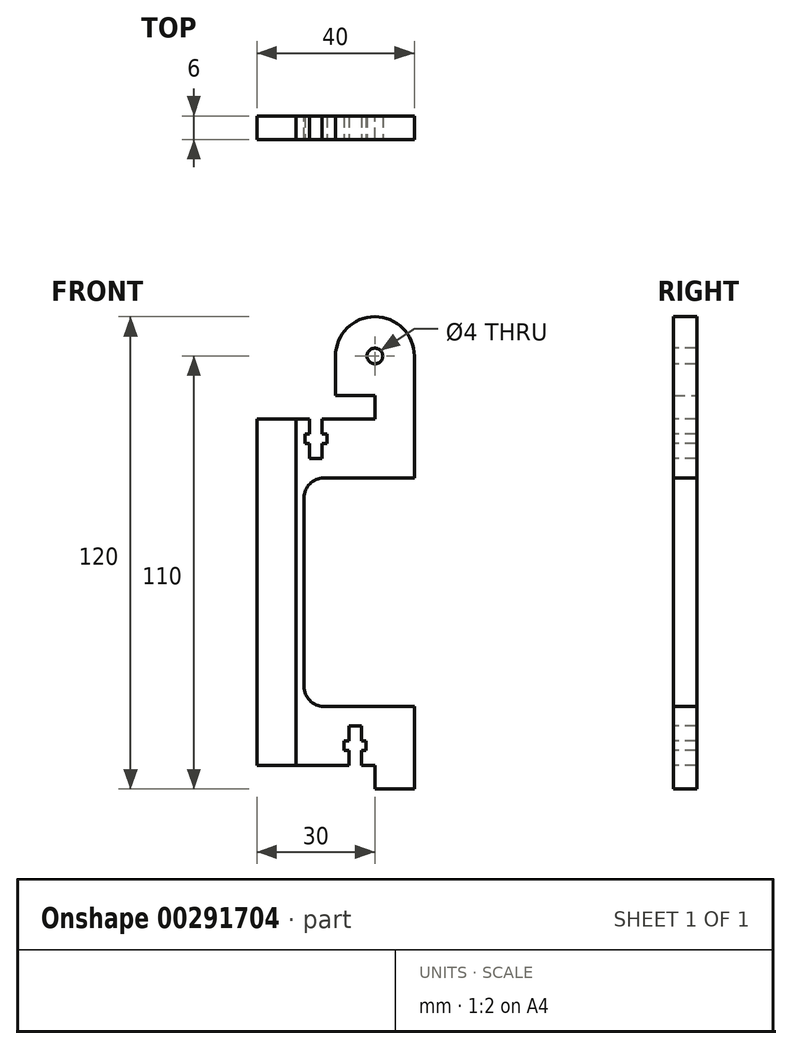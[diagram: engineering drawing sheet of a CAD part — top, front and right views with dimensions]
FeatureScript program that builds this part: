
annotation { "Feature Type Name" : "Feature", "Feature Type Description" : "" }
export const myFeature = defineFeature(function(context is Context, id is Id, definition is map)
    precondition{}
    {
        {
            var Q0;
            Q0=qCreatedBy(makeId("Front.planeOp"),FACE);
            var sketch = newSketch(context, id + "F0", { "sketchPlane" : qUnion([Q0])});
            skLineSegment(sketch, "E0", {"start": v(0, 0) * mm, "end": v(-10, 0) * mm});
            skLineSegment(sketch, "E1", {"start": v(-10, 0) * mm, "end": v(-10, 6) * mm});
            skLineSegment(sketch, "E2", {"start": v(-10, 6) * mm, "end": v(-30, 6) * mm});
            skLineSegment(sketch, "E3", {"start": v(-30, 6) * mm, "end": v(-30, 94) * mm});
            skLineSegment(sketch, "E4", {"start": v(-30, 94) * mm, "end": v(-10, 94) * mm});
            skLineSegment(sketch, "E5", {"start": v(-10, 94) * mm, "end": v(-10, 100) * mm});
            skLineSegment(sketch, "E6", {"start": v(0, 110) * mm, "end": v(0, 0) * mm});
            skLineSegment(sketch, "E7", {"start": v(-10, 100) * mm, "end": v(-20, 100) * mm});
            skLineSegment(sketch, "E8", {"start": v(-20, 100) * mm, "end": v(-20, 110) * mm});
            skArc(sketch, "E9", {"start": v(0, 110) * mm, "mid": v(-10, 120) * mm, "end": v(-20, 110) * mm});
            skLineSegment(sketch, "E10", {"start": v(-20, 110) * mm, "end": v(0, 110) * mm, "construction": true});
            skSolve(sketch);
        }
        {
            var Q0;
            Q0=qSketchRegion(id+"F0",true);
            extrude(context, id + "F1", {"entities" : qUnion([Q0]), "depth" : 6 * mm});
        }
        {
            var Q0;
            Q0=makeQuery(id+"F1.opExtrude","CAP_FACE",FACE,{"disambiguationData":[OSD([sQuery(id+"F0.wireOp",EDGE,"E0"),sQuery(id+"F0.wireOp",EDGE,"E1"),sQuery(id+"F0.wireOp",EDGE,"E2"),sQuery(id+"F0.wireOp",EDGE,"E3"),sQuery(id+"F0.wireOp",EDGE,"E4"),sQuery(id+"F0.wireOp",EDGE,"E5"),sQuery(id+"F0.wireOp",EDGE,"Jmk1pW6G-ZqLD-Fl2S-BXqT-ifLrlO1WaDic"),sQuery(id+"F0.wireOp",EDGE,"E6")])],"isStart":false});
            var sketch = newSketch(context, id + "F2", { "sketchPlane" : qUnion([Q0])});
            skLineSegment(sketch, "E11", {"start": v(-30, 50) * mm, "end": v(0, 50) * mm, "construction": true});
            skLineSegment(sketch, "E12", {"start": v(-10, 6) * mm, "end": v(-10, 94) * mm, "construction": true});
            skLineSegment(sketch, "E13", {"start": v(-15, 6) * mm, "end": v(-15, 50) * mm, "construction": true});
            skLineSegment(sketch, "E14", {"start": v(-15, 6) * mm, "end": v(-16.6, 6) * mm});
            skLineSegment(sketch, "E15", {"start": v(-16.6, 6) * mm, "end": v(-16.6, 9.75) * mm});
            skLineSegment(sketch, "E16", {"start": v(-16.6, 9.75) * mm, "end": v(-17.8, 9.75) * mm});
            skLineSegment(sketch, "E17", {"start": v(-17.8, 9.75) * mm, "end": v(-17.8, 12.25) * mm});
            skLineSegment(sketch, "E18", {"start": v(-17.8, 12.25) * mm, "end": v(-16.6, 12.25) * mm});
            skLineSegment(sketch, "E19", {"start": v(-16.6, 12.25) * mm, "end": v(-16.6, 16) * mm});
            skLineSegment(sketch, "E20", {"start": v(-16.6, 16) * mm, "end": v(-15, 16) * mm});
            skLineSegment(sketch, "E21.MirrorCS", {"start": v(-12.2, 12.25) * mm, "end": v(-13.4, 12.25) * mm});
            skLineSegment(sketch, "E22.MirrorCS", {"start": v(-12.2, 9.75) * mm, "end": v(-12.2, 12.25) * mm});
            skLineSegment(sketch, "E23.MirrorCS", {"start": v(-13.4, 12.25) * mm, "end": v(-13.4, 16) * mm});
            skLineSegment(sketch, "E24.MirrorCS", {"start": v(-13.4, 16) * mm, "end": v(-15, 16) * mm});
            skLineSegment(sketch, "E25.MirrorCS", {"start": v(-13.4, 9.75) * mm, "end": v(-12.2, 9.75) * mm});
            skLineSegment(sketch, "E26.MirrorCS", {"start": v(-15, 6) * mm, "end": v(-13.4, 6) * mm});
            skLineSegment(sketch, "E27.MirrorCS", {"start": v(-13.4, 6) * mm, "end": v(-13.4, 9.75) * mm});
            skLineSegment(sketch, "E28.MirrorCS", {"start": v(-10, 34) * mm, "end": v(-10, -54) * mm, "construction": true});
            skLineSegment(sketch, "E29", {"start": v(-25, 94) * mm, "end": v(-25, 50) * mm, "construction": true});
            skLineSegment(sketch, "E30", {"start": v(-25, 94) * mm, "end": v(-26.6, 94) * mm});
            skLineSegment(sketch, "E31", {"start": v(-26.6, 94) * mm, "end": v(-26.6, 90.25) * mm});
            skLineSegment(sketch, "E32", {"start": v(-26.6, 90.25) * mm, "end": v(-27.8, 90.25) * mm});
            skLineSegment(sketch, "E33", {"start": v(-27.8, 90.25) * mm, "end": v(-27.8, 87.75) * mm});
            skLineSegment(sketch, "E34", {"start": v(-27.8, 87.75) * mm, "end": v(-26.6, 87.75) * mm});
            skLineSegment(sketch, "E35", {"start": v(-26.6, 87.75) * mm, "end": v(-26.6, 84) * mm});
            skLineSegment(sketch, "E36", {"start": v(-26.6, 84) * mm, "end": v(-25, 84) * mm});
            skLineSegment(sketch, "E37.MirrorCS", {"start": v(-23.4, 84) * mm, "end": v(-25, 84) * mm});
            skLineSegment(sketch, "E38.MirrorCS", {"start": v(-23.4, 87.75) * mm, "end": v(-23.4, 84) * mm});
            skLineSegment(sketch, "E39.MirrorCS", {"start": v(-22.2, 87.75) * mm, "end": v(-23.4, 87.75) * mm});
            skLineSegment(sketch, "E40.MirrorCS", {"start": v(-22.2, 90.25) * mm, "end": v(-22.2, 87.75) * mm});
            skLineSegment(sketch, "E41.MirrorCS", {"start": v(-23.4, 90.25) * mm, "end": v(-22.2, 90.25) * mm});
            skLineSegment(sketch, "E42.MirrorCS", {"start": v(-25, 94) * mm, "end": v(-23.4, 94) * mm});
            skLineSegment(sketch, "E43.MirrorCS", {"start": v(-23.4, 94) * mm, "end": v(-23.4, 90.25) * mm});
            skSolve(sketch);
        }
        {
            var Q0;
            Q0=qSketchRegion(id+"F2",true);
            extrude(context, id + "F3", {"entities" : qUnion([Q0]), "operationType" : NewBodyOperationType.REMOVE, "endBound" : BoundingType.THROUGH_ALL, "oppositeDirection" : true, "depth" : 25 * mm});
        }
        {
            var Q0;
            Q0=makeQuery(id+"F1.opExtrude","CAP_FACE",FACE,{"disambiguationData":[OSD([sQuery(id+"F0.wireOp",EDGE,"E0"),sQuery(id+"F0.wireOp",EDGE,"E1"),sQuery(id+"F0.wireOp",EDGE,"E2"),sQuery(id+"F0.wireOp",EDGE,"E3"),sQuery(id+"F0.wireOp",EDGE,"E4"),sQuery(id+"F0.wireOp",EDGE,"E5"),sQuery(id+"F0.wireOp",EDGE,"E6"),sQuery(id+"F0.wireOp",EDGE,"E7"),sQuery(id+"F0.wireOp",EDGE,"E8"),sQuery(id+"F0.wireOp",EDGE,"E9")])],"isStart":false});
            var sketch = newSketch(context, id + "F4", { "sketchPlane" : qUnion([Q0])});
            skLineSegment(sketch, "E44", {"start": v(-20, 110) * mm, "end": v(0, 110) * mm, "construction": true});
            skCircle(sketch, "E45", {"center": v(-10, 110) * mm, "radius": 2 * mm});
            skSolve(sketch);
        }
        {
            var Q0;
            Q0=qSketchRegion(id+"F4",true);
            extrude(context, id + "F5", {"entities" : qUnion([Q0]), "operationType" : NewBodyOperationType.REMOVE, "endBound" : BoundingType.THROUGH_ALL, "oppositeDirection" : true, "depth" : 25 * mm});
        }
        {
            var Q0;
            Q0=makeQuery(id+"F1.opExtrude","CAP_FACE",FACE,{"disambiguationData":[OSD([sQuery(id+"F0.wireOp",EDGE,"E0"),sQuery(id+"F0.wireOp",EDGE,"E1"),sQuery(id+"F0.wireOp",EDGE,"E2"),sQuery(id+"F0.wireOp",EDGE,"E3"),sQuery(id+"F0.wireOp",EDGE,"E4"),sQuery(id+"F0.wireOp",EDGE,"E5"),sQuery(id+"F0.wireOp",EDGE,"E6"),sQuery(id+"F0.wireOp",EDGE,"E7"),sQuery(id+"F0.wireOp",EDGE,"E8"),sQuery(id+"F0.wireOp",EDGE,"E9")])],"isStart":false});
            var sketch = newSketch(context, id + "F6", { "sketchPlane" : qUnion([Q0])});
            skLineSegment(sketch, "E46.bottom", {"start": v(0, 79) * mm, "end": v(-5, 79) * mm});
            skLineSegment(sketch, "E46.top", {"start": v(0, 21) * mm, "end": v(-5, 21) * mm});
            skLineSegment(sketch, "E46.left", {"start": v(0, 79) * mm, "end": v(0, 21) * mm});
            skLineSegment(sketch, "E46.right", {"start": v(-5, 79) * mm, "end": v(-5, 21) * mm});
            skSolve(sketch);
        }
        {
            var Q0;
            Q0 = qSketchRegion(id + "F6", true);
            extrude(context, id + "F7", {"entities" : qUnion([Q0]), "operationType" : NewBodyOperationType.REMOVE, "endBound" : BoundingType.THROUGH_ALL, "oppositeDirection" : true, "offsetDistance" : 25 * mm, "depth" : 25 * mm});
        }
        {
            var Q0;
            Q0=makeQuery(id+"F7.boolean.opBoolean","COPY",EDGE,{"derivedFrom":makeQuery(id+"F7.opExtrude","SWEPT_EDGE",EDGE,{"disambiguationData":[OSD([sQuery(id+"F6.wireOp",EDGE,"E46.bottom"),sQuery(id+"F6.wireOp",EDGE,"E46.right")])]})});
            var Q1;
            Q1=makeQuery(id+"F7.boolean.opBoolean","COPY",EDGE,{"derivedFrom":makeQuery(id+"F7.opExtrude","SWEPT_EDGE",EDGE,{"disambiguationData":[OSD([sQuery(id+"F0.wireOp",EDGE,"E6"),sQuery(id+"F6.wireOp",EDGE,"E46.bottom"),sQuery(id+"F6.wireOp",EDGE,"E46.left")])]})});
            var Q2;
            Q2=makeQuery(id+"F7.boolean.opBoolean","COPY",EDGE,{"derivedFrom":makeQuery(id+"F7.opExtrude","SWEPT_EDGE",EDGE,{"disambiguationData":[OSD([sQuery(id+"F6.wireOp",EDGE,"E46.top"),sQuery(id+"F6.wireOp",EDGE,"E46.right")])]})});
            var Q3;
            Q3=makeQuery(id+"F7.boolean.opBoolean","COPY",EDGE,{"derivedFrom":makeQuery(id+"F7.opExtrude","SWEPT_EDGE",EDGE,{"disambiguationData":[OSD([sQuery(id+"F0.wireOp",EDGE,"E6"),sQuery(id+"F6.wireOp",EDGE,"E46.top"),sQuery(id+"F6.wireOp",EDGE,"E46.left")])]})});
            fillet(context, id + "F8", {"entities" : qUnion([Q0, Q1, Q2, Q3]), "radius" : 2.5 * mm, "tangentPropagation" : true, "allowEdgeOverflow" : false});
        }
        {
            var Q0;
            Q0=qCreatedBy(makeId("Front.planeOp"),FACE);
            var sketch = newSketch(context, id + "F9", { "sketchPlane" : qUnion([Q0])});
            skLineSegment(sketch, "E47", {"start": v(0, 0) * mm, "end": v(-10, 0) * mm});
            skLineSegment(sketch, "E48", {"start": v(-10, 0) * mm, "end": v(-10, 6) * mm});
            skLineSegment(sketch, "E49", {"start": v(-10, 6) * mm, "end": v(-40, 6) * mm});
            skLineSegment(sketch, "E50", {"start": v(-40, 6) * mm, "end": v(-40, 94) * mm});
            skLineSegment(sketch, "E51", {"start": v(-40, 94) * mm, "end": v(-10, 94) * mm});
            skLineSegment(sketch, "E52", {"start": v(-10, 94) * mm, "end": v(-10, 100) * mm});
            skLineSegment(sketch, "E53", {"start": v(0, 110) * mm, "end": v(0, 0) * mm});
            skLineSegment(sketch, "E54", {"start": v(-10, 100) * mm, "end": v(-20, 100) * mm});
            skLineSegment(sketch, "E55", {"start": v(-20, 100) * mm, "end": v(-20, 110) * mm});
            skArc(sketch, "E56", {"start": v(0, 110) * mm, "mid": v(-10, 120) * mm, "end": v(-20, 110) * mm});
            skLineSegment(sketch, "E57", {"start": v(-20, 110) * mm, "end": v(0, 110) * mm, "construction": true});
            skSolve(sketch);
        }
        {
            var Q0;
            Q0=makeQuery(id+"F9.imprint","IMPRINT",FACE,{"disambiguationData":[TD([[makeQuery(id+"F9.imprint","IMPRINT",EDGE,{"derivedFrom":sQuery(id+"F9.wireOp",EDGE,"E47")}),-1.0]])]});
            extrude(context, id + "F10", {"entities" : qUnion([Q0]), "depth" : 6 * mm, "offsetDistance" : 25 * mm});
        }
        {
            var Q0;
            Q0 = qSketchRegion(id + "F2", true);
            extrude(context, id + "F11", {"entities" : qUnion([Q0]), "operationType" : NewBodyOperationType.REMOVE, "oppositeDirection" : true, "depth" : 25 * mm, "offsetDistance" : 25 * mm});
        }
        {
            var Q0;
            Q0=qCreatedBy(makeId("Front.planeOp"),FACE);
            var sketch = newSketch(context, id + "F12", { "sketchPlane" : qUnion([Q0])});
            skLineSegment(sketch, "E58.bottom", {"start": v(0, 79) * mm, "end": v(-28, 79) * mm});
            skLineSegment(sketch, "E58.top", {"start": v(0, 21) * mm, "end": v(-28, 21) * mm});
            skLineSegment(sketch, "E58.left", {"start": v(0, 79) * mm, "end": v(0, 21) * mm});
            skLineSegment(sketch, "E58.right", {"start": v(-28, 79) * mm, "end": v(-28, 21) * mm});
            skSolve(sketch);
        }
        {
            var Q0;
            Q0 = qSketchRegion(id + "F12", true);
            extrude(context, id + "F13", {"entities" : qUnion([Q0]), "operationType" : NewBodyOperationType.REMOVE, "endBound" : BoundingType.UP_TO_NEXT, "depth" : 25 * mm, "offsetDistance" : 25 * mm});
        }
        {
            var Q0;
            Q0=makeQuery(id+"F13.boolean.opBoolean","COPY",EDGE,{"derivedFrom":makeQuery(id+"F13.opExtrude","SWEPT_EDGE",EDGE,{"disambiguationData":[OSD([sQuery(id+"F12.wireOp",EDGE,"E58.bottom"),sQuery(id+"F12.wireOp",EDGE,"E58.left")])]})});
            var Q1;
            Q1=makeQuery(id+"F13.boolean.opBoolean","COPY",EDGE,{"derivedFrom":makeQuery(id+"F13.opExtrude","SWEPT_EDGE",EDGE,{"disambiguationData":[OSD([sQuery(id+"F12.wireOp",EDGE,"E58.top"),sQuery(id+"F12.wireOp",EDGE,"E58.left")])]})});
            var Q2;
            Q2=makeQuery(id+"F13.boolean.opBoolean","COPY",EDGE,{"derivedFrom":makeQuery(id+"F13.opExtrude","SWEPT_EDGE",EDGE,{"disambiguationData":[OSD([sQuery(id+"F12.wireOp",EDGE,"E58.top"),sQuery(id+"F12.wireOp",EDGE,"E58.right")])]})});
            var Q3;
            Q3=makeQuery(id+"F13.boolean.opBoolean","COPY",EDGE,{"derivedFrom":makeQuery(id+"F13.opExtrude","SWEPT_EDGE",EDGE,{"disambiguationData":[OSD([sQuery(id+"F12.wireOp",EDGE,"E58.bottom"),sQuery(id+"F12.wireOp",EDGE,"E58.right")])]})});
            fillet(context, id + "F14", {"entities" : qUnion([Q0, Q1, Q2, Q3]), "tangentPropagation" : true, "radius" : 5 * mm, "defaultsChanged" : false, "vertexSettings" : [], "allowEdgeOverflow" : false});
        }
    });
